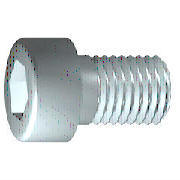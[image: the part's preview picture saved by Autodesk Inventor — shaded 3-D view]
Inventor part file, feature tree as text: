
AUTODESK INVENTOR PART (.ipt)
format: ipt  version: 2017 (Build 210142000, 142)  size: 188,416 bytes
history: native  units: mm (DEFAULTED — no unit token found)
features: sketch x2, extrude x1, plane x1, fillet x1
ambient origin geometry x7: Origin, YZ Plane, XY Plane, X Axis, Y Axis, Z Axis, Center Point
bodies: Solid1 (feature_tree), Body (feature_tree)
feature tree (5):
  extrude  "Slot"  Depth=2.5mm
  plane  "Work Plane1"
  fillet  "Fillet2"  Radius=2.5mm
  sketch  "Sketch1"  dims[d1=8.823947mm d2=0.276153mm d3=2.5mm]
  sketch  "Sketch2"  dims[d4=1.25mm d5=60.0deg d6=2.5mm d7=2.5mm d8=2.309401mm d9=4.5mm d10=90.0deg d11=10.0mm d12=0.0mm d13=8.823947mm d14=0.0mm d15=0.276052mm d16=0.276053mm d17=0.25mm d19=0.0mm d26=10.0mm d27=45.0deg d28=0.0mm d29=0.0mm d30=0.1mm]
